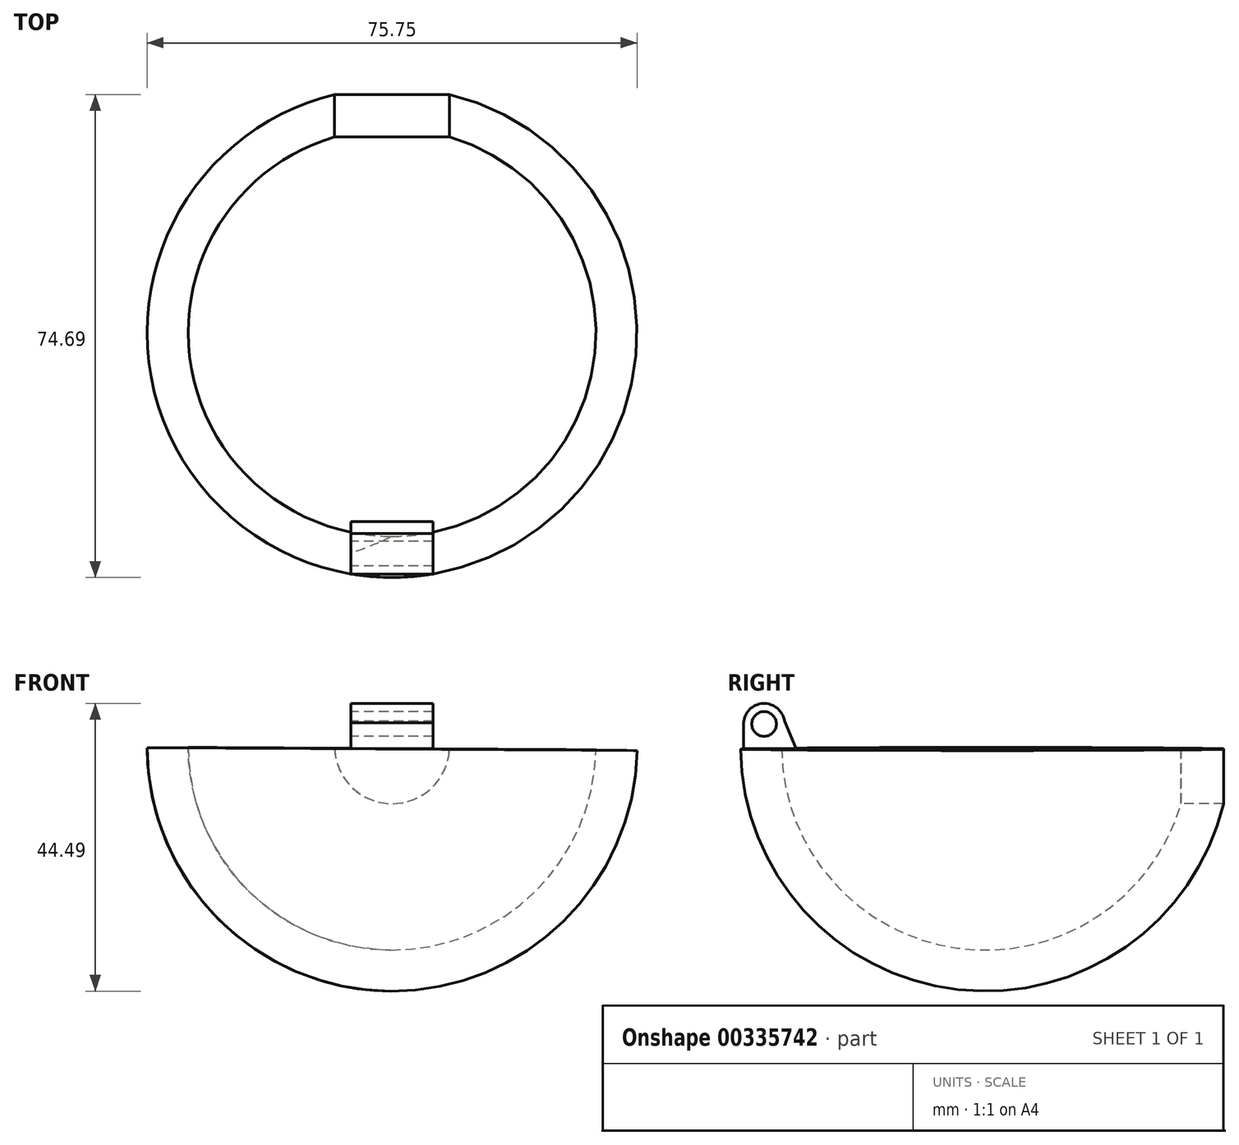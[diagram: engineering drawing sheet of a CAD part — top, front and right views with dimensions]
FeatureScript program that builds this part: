
annotation { "Feature Type Name" : "Feature", "Feature Type Description" : "" }
export const myFeature = defineFeature(function(context is Context, id is Id, definition is map)
    precondition{}
    {
        {
            var Q0;
            Q0=qCreatedBy(makeId("Front.planeOp"),FACE);
            var sketch = newSketch(context, id + "F0", { "sketchPlane" : qUnion([Q0])});
            skArc(sketch, "E0.0", {"start": v(-31.53, -0.19) * mm, "mid": v(-22.3, -22.3) * mm, "end": v(-0.19, -31.53) * mm});
            skArc(sketch, "E1.0", {"start": v(-37.88, -0.22) * mm, "mid": v(-26.78, -26.78) * mm, "end": v(-0.22, -37.88) * mm});
            skLineSegment(sketch, "E2", {"start": v(-37.88, -0.22) * mm, "end": v(-31.53, -0.19) * mm});
            skLineSegment(sketch, "E3", {"start": v(-0.19, -31.53) * mm, "end": v(-0.22, -37.88) * mm});
            skSolve(sketch);
        }
        {
            var Q0;
            Q0=makeQuery(id+"F0.imprint","IMPRINT",FACE,{"disambiguationData":[TD([[makeQuery(id+"F0.imprint","IMPRINT",EDGE,{"derivedFrom":sQuery(id+"F0.wireOp",EDGE,"E0.0")}),-1.0]])]});
            var Q1;
            Q1=sQuery(id+"F0.wireOp",EDGE,"E3");
            revolve(context, id + "F1", {"entities" : qUnion([Q0]), "axis" : qUnion([Q1]), "revolveType" : RevolveType.FULL});
        }
        {
            var Q0;
            Q0=qCreatedBy(makeId("Front.planeOp"),FACE);
            var sketch = newSketch(context, id + "F2", { "sketchPlane" : qUnion([Q0])});
            skCircle(sketch, "E4", {"center": v(0, 0) * mm, "radius": 8.9 * mm});
            skSolve(sketch);
        }
        {
            var Q0;
            Q0=makeQuery(id+"F2.imprint","IMPRINT",FACE,{"disambiguationData":[TD([[makeQuery(id+"F2.imprint","IMPRINT",EDGE,{"derivedFrom":sQuery(id+"F2.wireOp",EDGE,"E4")}),1.0]])]});
            extrude(context, id + "F3", {"entities" : qUnion([Q0]), "operationType" : NewBodyOperationType.REMOVE, "endBound" : BoundingType.THROUGH_ALL, "oppositeDirection" : true, "depth" : 25.4 * mm});
        }
        {
            var Q0;
            Q0=qCreatedBy(makeId("Right.planeOp"),FACE);
            var sketch = newSketch(context, id + "F4", { "sketchPlane" : qUnion([Q0])});
            skLineSegment(sketch, "E5", {"start": v(-31.52, -0.37) * mm, "end": v(-40.13, -0.37) * mm});
            skPoint(sketch, "E5.endSnap0", {"position": v(-32.31, -0.37) * mm});
            skPoint(sketch, "E6.orphan", {"position": v(30.25, -0.32) * mm});
            skPoint(sketch, "E7.0.end.orphan", {"position": v(30.25, -0.42) * mm});
            skCircle(sketch, "E8", {"center": v(-34.22, 3.44) * mm, "radius": 1.9 * mm});
            skArc(sketch, "E9.0", {"start": v(-31.08, 3.9) * mm, "mid": v(-34.54, 6.6) * mm, "end": v(-37.39, 3.26) * mm});
            skLineSegment(sketch, "E10", {"start": v(-37.39, 3.61) * mm, "end": v(-37.39, -0.37) * mm});
            skLineSegment(sketch, "E11", {"start": v(-37.39, -0.37) * mm, "end": v(-29.25, -0.37) * mm});
            skLineSegment(sketch, "E12", {"start": v(-29.25, -0.37) * mm, "end": v(-31.08, 3.9) * mm});
            skSolve(sketch);
        }
        {
            var Q0;
            Q0=makeQuery(id+"F4.imprint","IMPRINT",FACE,{"disambiguationData":[TD([[makeQuery(id+"F4.imprint","IMPRINT",EDGE,{"derivedFrom":sQuery(id+"F4.wireOp",EDGE,"E8")}),-1.0]])]});
            extrude(context, id + "F5", {"entities" : qUnion([Q0]), "operationType" : NewBodyOperationType.ADD, "endBound" : BoundingType.SYMMETRIC, "depth" : 12.7 * mm});
        }
    });
